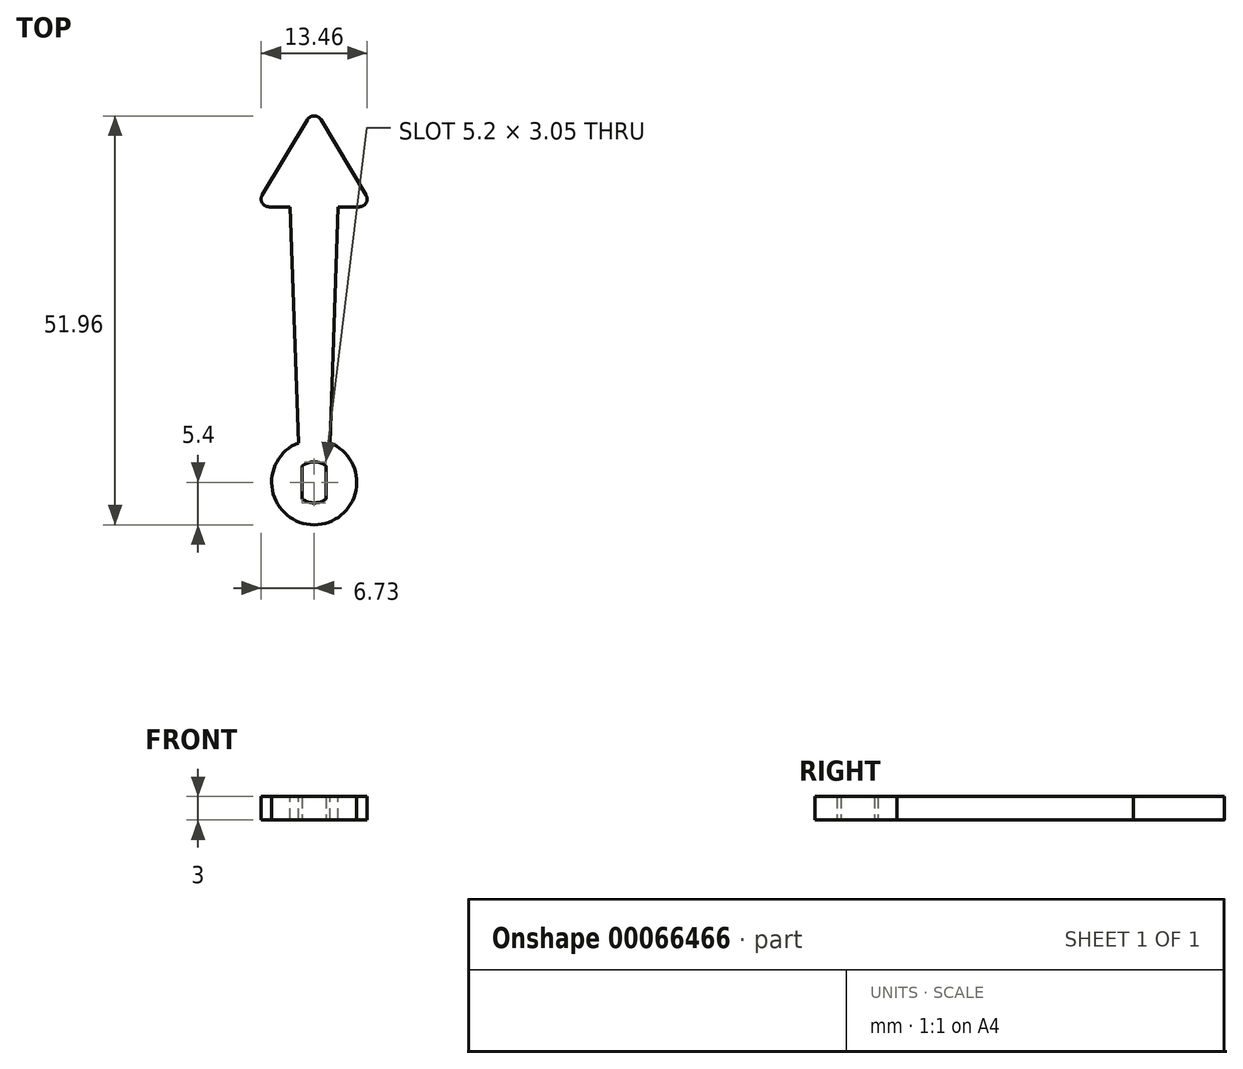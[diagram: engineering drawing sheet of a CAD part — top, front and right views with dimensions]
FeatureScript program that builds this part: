
annotation { "Feature Type Name" : "Feature", "Feature Type Description" : "" }
export const myFeature = defineFeature(function(context is Context, id is Id, definition is map)
    precondition{}
    {
        {
            var Q0;
            Q0=qCreatedBy(makeId("Top.planeOp"),FACE);
            var sketch = newSketch(context, id + "F0", { "sketchPlane" : qUnion([Q0])});
            skCircle(sketch, "E0", {"center": v(0, 0) * mm, "radius": 2.6 * mm});
            skCircle(sketch, "E1", {"center": v(0, 0) * mm, "radius": 5.4 * mm});
            skLineSegment(sketch, "E2", {"start": v(-1.53, 2.1) * mm, "end": v(-1.53, -2.1) * mm});
            skLineSegment(sketch, "E3", {"start": v(1.52, 2.1) * mm, "end": v(1.52, -2.1) * mm});
            skSolve(sketch);
        }
        {
            var Q0;
            Q0=makeQuery(id+"F0.imprint","IMPRINT",FACE,{"disambiguationData":[TD([[makeQuery(id+"F0.imprint","IMPRINT",EDGE,{"derivedFrom":sQuery(id+"F0.wireOp",EDGE,"E1")}),1.0]])]});
            var Q1;
            {var subQ0=sQuery(id+"F0.wireOp",EDGE,"E3");Q1=makeQuery(id+"F0.imprint","IMPRINT",FACE,{"disambiguationData":[TD([[makeQuery(id+"F0.imprint","IMPRINT",EDGE,{"derivedFrom":subQ0}),1.0]])]});}
            var Q2;
            {var subQ0=sQuery(id+"F0.wireOp",EDGE,"E2");Q2=makeQuery(id+"F0.imprint","IMPRINT",FACE,{"disambiguationData":[TD([[makeQuery(id+"F0.imprint","IMPRINT",EDGE,{"derivedFrom":subQ0}),-1.0]])]});}
            extrude(context, id + "F1", {"entities" : qUnion([Q0, Q1, Q2]), "endBound" : BoundingType.SYMMETRIC, "depth" : 3 * mm});
        }
        {
            var Q0;
            Q0=makeQuery(id+"F1.opExtrude","CAP_FACE",FACE,{"disambiguationData":[OSD([sQuery(id+"F0.wireOp",EDGE,"E0"),sQuery(id+"F0.wireOp",EDGE,"E1"),sQuery(id+"F0.wireOp",EDGE,"E2"),sQuery(id+"F0.wireOp",EDGE,"E3")])],"isStart":false});
            var sketch = newSketch(context, id + "F2", { "sketchPlane" : qUnion([Q0])});
            skLineSegment(sketch, "E4", {"start": v(0, 0) * mm, "end": v(0, 35) * mm, "construction": true});
            skPoint(sketch, "E4.endSnap0", {"position": v(0, 2.6) * mm});
            skLineSegment(sketch, "E5", {"start": v(0, 5.02) * mm, "end": v(2, 5.02) * mm});
            skLineSegment(sketch, "E6", {"start": v(0, 35) * mm, "end": v(3.05, 35) * mm});
            skLineSegment(sketch, "E7", {"start": v(3.05, 35) * mm, "end": v(2, 5.02) * mm});
            skLineSegment(sketch, "E8.MirrorCS", {"start": v(0, 35) * mm, "end": v(-3.05, 35) * mm});
            skLineSegment(sketch, "E9.MirrorCS", {"start": v(-3.05, 35) * mm, "end": v(-2, 5.02) * mm});
            skLineSegment(sketch, "E10.MirrorCS", {"start": v(0, 5.02) * mm, "end": v(-2, 5.02) * mm});
            skSolve(sketch);
        }
        {
            var Q0;
            Q0=makeQuery(id+"F2.imprint","IMPRINT",FACE,{"disambiguationData":[TD([[makeQuery(id+"F2.imprint","IMPRINT",EDGE,{"derivedFrom":sQuery(id+"F2.wireOp",EDGE,"E6")}),-1.0]])]});
            var Q1;
            Q1=makeQuery(id+"F1.opExtrude","CAP_FACE",FACE,{"disambiguationData":[OSD([sQuery(id+"F0.wireOp",EDGE,"E0"),sQuery(id+"F0.wireOp",EDGE,"E1"),sQuery(id+"F0.wireOp",EDGE,"E2"),sQuery(id+"F0.wireOp",EDGE,"E3")])],"isStart":true});
            extrude(context, id + "F3", {"entities" : qUnion([Q0]), "operationType" : NewBodyOperationType.ADD, "endBound" : BoundingType.UP_TO_SURFACE, "oppositeDirection" : true, "endBoundEntityFace" : qUnion([Q1]), "depth" : 25 * mm});
        }
        {
            var Q0;
            {var subQ0=sQuery(id+"F0.wireOp",EDGE,"E1");Q0=makeQuery(id+"F3.boolean.opBoolean","MERGE",FACE,{"derivedFrom":[makeQuery(id+"F1.opExtrude","CAP_FACE",FACE,{"disambiguationData":[OSD([sQuery(id+"F0.wireOp",EDGE,"E0"),subQ0,sQuery(id+"F0.wireOp",EDGE,"E2"),sQuery(id+"F0.wireOp",EDGE,"E3")])],"isStart":false}),makeQuery(id+"F3.opExtrude","CAP_FACE",FACE,{"disambiguationData":[OSD([subQ0,sQuery(id+"F2.wireOp",EDGE,"E6"),sQuery(id+"F2.wireOp",EDGE,"E7"),sQuery(id+"F2.wireOp",EDGE,"E8.MirrorCS"),sQuery(id+"F2.wireOp",EDGE,"E9.MirrorCS")])],"isStart":true})]});}
            var sketch = newSketch(context, id + "F4", { "sketchPlane" : qUnion([Q0])});
            skLineSegment(sketch, "E11", {"start": v(0, 35) * mm, "end": v(0, 47.5) * mm, "construction": true});
            skLineSegment(sketch, "E12", {"start": v(-7.5, 35) * mm, "end": v(7.5, 35) * mm});
            skLineSegment(sketch, "E13", {"start": v(-7.5, 35) * mm, "end": v(0, 47.5) * mm});
            skLineSegment(sketch, "E14", {"start": v(7.5, 35) * mm, "end": v(0, 47.5) * mm});
            skSolve(sketch);
        }
        {
            var Q0;
            {var subQ0=sQuery(id+"F4.wireOp",EDGE,"E13");Q0=makeQuery(id+"F4.imprint","IMPRINT",FACE,{"disambiguationData":[TD([[makeQuery(id+"F4.imprint","IMPRINT",EDGE,{"derivedFrom":subQ0}),-1.0]])]});}
            var Q1;
            {var subQ0=sQuery(id+"F0.wireOp",EDGE,"E1");Q1=makeQuery(id+"F3.boolean.opBoolean","MERGE",FACE,{"derivedFrom":[makeQuery(id+"F1.opExtrude","CAP_FACE",FACE,{"disambiguationData":[OSD([sQuery(id+"F0.wireOp",EDGE,"E0"),subQ0,sQuery(id+"F0.wireOp",EDGE,"E2"),sQuery(id+"F0.wireOp",EDGE,"E3")])],"isStart":true}),makeQuery(id+"F3.opExtrude","CAP_FACE",FACE,{"disambiguationData":[OSD([subQ0,sQuery(id+"F2.wireOp",EDGE,"E6"),sQuery(id+"F2.wireOp",EDGE,"E7"),sQuery(id+"F2.wireOp",EDGE,"E8.MirrorCS"),sQuery(id+"F2.wireOp",EDGE,"E9.MirrorCS")])],"isStart":false})]});}
            extrude(context, id + "F5", {"entities" : qUnion([Q0]), "operationType" : NewBodyOperationType.ADD, "endBound" : BoundingType.UP_TO_SURFACE, "oppositeDirection" : true, "endBoundEntityFace" : qUnion([Q1]), "depth" : 25 * mm});
        }
        {
            var Q0;
            Q0=makeQuery(id+"F5.opExtrude","SWEPT_EDGE",EDGE,{"disambiguationData":[OSD([sQuery(id+"F4.wireOp",EDGE,"E12"),sQuery(id+"F4.wireOp",EDGE,"E13")])]});
            var Q1;
            Q1=makeQuery(id+"F5.opExtrude","SWEPT_EDGE",EDGE,{"disambiguationData":[OSD([sQuery(id+"F4.wireOp",EDGE,"E13"),sQuery(id+"F4.wireOp",EDGE,"E14")])]});
            var Q2;
            Q2=makeQuery(id+"F5.opExtrude","SWEPT_EDGE",EDGE,{"disambiguationData":[OSD([sQuery(id+"F4.wireOp",EDGE,"E12"),sQuery(id+"F4.wireOp",EDGE,"E14")])]});
            fillet(context, id + "F6", {"entities" : qUnion([Q0, Q1, Q2]), "radius" : 1 * mm, "tangentPropagation" : true, "allowEdgeOverflow" : false});
        }
    });
